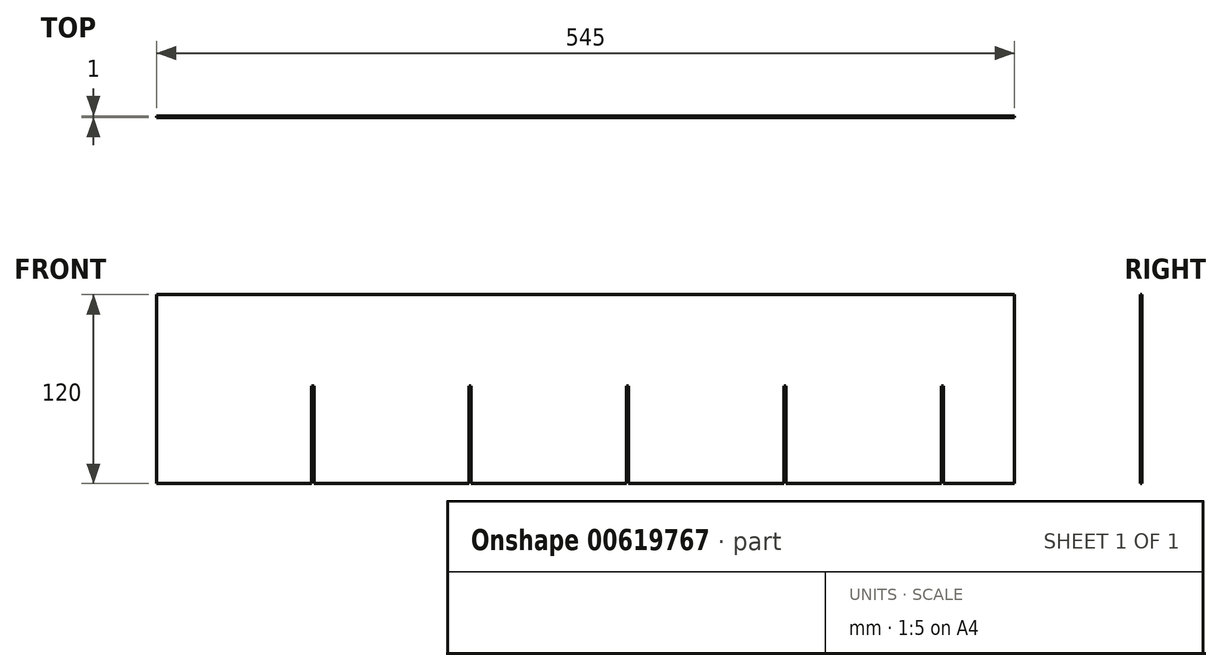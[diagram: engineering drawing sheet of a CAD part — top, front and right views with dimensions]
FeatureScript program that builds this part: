
annotation { "Feature Type Name" : "Feature", "Feature Type Description" : "" }
export const myFeature = defineFeature(function(context is Context, id is Id, definition is map)
    precondition{}
    {
        {
            var Q0;
            Q0=qCreatedBy(makeId("Front.planeOp"),FACE);
            var sketch = newSketch(context, id + "F0", { "sketchPlane" : qUnion([Q0])});
            skLineSegment(sketch, "E0", {"start": v(-67.02, -9.71) * mm, "end": v(31.48, -9.71) * mm});
            skLineSegment(sketch, "E1", {"start": v(31.48, -9.71) * mm, "end": v(31.48, 52.29) * mm});
            skLineSegment(sketch, "E2", {"start": v(31.48, 52.29) * mm, "end": v(32.98, 52.29) * mm});
            skLineSegment(sketch, "E3", {"start": v(32.98, 52.29) * mm, "end": v(32.98, -9.71) * mm});
            skLineSegment(sketch, "E4", {"start": v(32.98, -9.71) * mm, "end": v(131.48, -9.71) * mm});
            skLineSegment(sketch, "E5", {"start": v(131.48, -9.71) * mm, "end": v(131.48, 52.29) * mm});
            skLineSegment(sketch, "E6", {"start": v(131.48, 52.29) * mm, "end": v(132.98, 52.29) * mm});
            skLineSegment(sketch, "E7", {"start": v(132.98, 52.29) * mm, "end": v(132.98, -9.71) * mm});
            skLineSegment(sketch, "E8", {"start": v(132.98, -9.71) * mm, "end": v(231.48, -9.71) * mm});
            skLineSegment(sketch, "E9", {"start": v(231.48, -9.71) * mm, "end": v(231.48, 52.29) * mm});
            skLineSegment(sketch, "E10", {"start": v(231.48, 52.29) * mm, "end": v(232.98, 52.29) * mm});
            skLineSegment(sketch, "E11", {"start": v(232.98, 52.29) * mm, "end": v(232.98, -9.71) * mm});
            skLineSegment(sketch, "E12", {"start": v(232.98, -9.71) * mm, "end": v(331.48, -9.71) * mm});
            skLineSegment(sketch, "E13", {"start": v(331.48, -9.71) * mm, "end": v(331.48, 52.29) * mm});
            skLineSegment(sketch, "E14", {"start": v(331.48, 52.29) * mm, "end": v(332.98, 52.29) * mm});
            skLineSegment(sketch, "E15", {"start": v(332.98, 52.29) * mm, "end": v(332.98, -9.71) * mm});
            skLineSegment(sketch, "E16", {"start": v(332.98, -9.71) * mm, "end": v(431.48, -9.71) * mm});
            skLineSegment(sketch, "E17", {"start": v(431.48, -9.71) * mm, "end": v(431.48, 52.29) * mm});
            skLineSegment(sketch, "E18", {"start": v(431.48, 52.29) * mm, "end": v(432.98, 52.29) * mm});
            skLineSegment(sketch, "E19", {"start": v(432.98, 52.29) * mm, "end": v(432.98, -9.71) * mm});
            skLineSegment(sketch, "E20", {"start": v(-67.02, -9.71) * mm, "end": v(-67.02, 110.29) * mm});
            skLineSegment(sketch, "E21", {"start": v(-67.02, 110.29) * mm, "end": v(477.98, 110.29) * mm});
            skLineSegment(sketch, "E22", {"start": v(477.98, 110.29) * mm, "end": v(477.98, -9.71) * mm});
            skLineSegment(sketch, "E23", {"start": v(432.98, -9.71) * mm, "end": v(477.98, -9.71) * mm});
            skSolve(sketch);
        }
        {
            var Q0;
            Q0=makeQuery(id+"F0.imprint","IMPRINT",FACE,{"disambiguationData":[TD([[makeQuery(id+"F0.imprint","IMPRINT",EDGE,{"derivedFrom":sQuery(id+"F0.wireOp",EDGE,"E0")}),1.0]])]});
            extrude(context, id + "F1", {"entities" : qUnion([Q0]), "depth" : 1 * mm, "offsetDistance" : 25 * mm});
        }
    });
